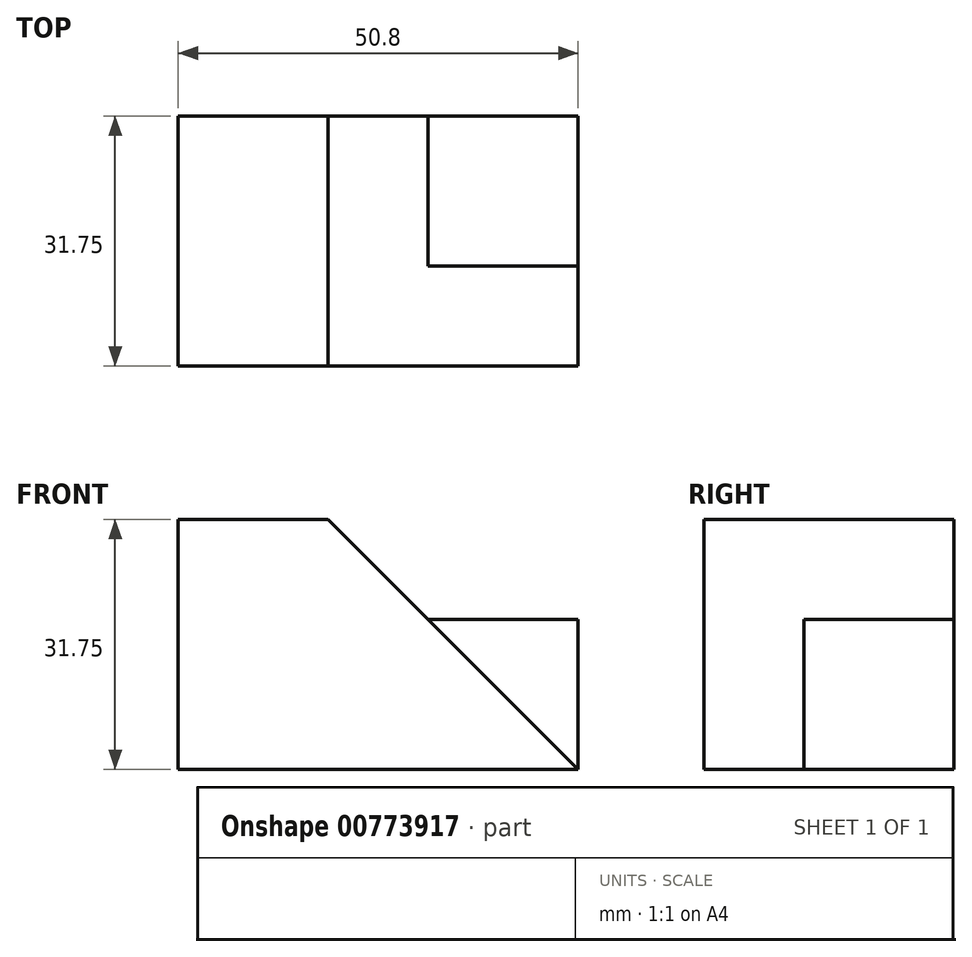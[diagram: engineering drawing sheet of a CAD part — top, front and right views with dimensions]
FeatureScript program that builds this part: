
annotation { "Feature Type Name" : "Feature", "Feature Type Description" : "" }
export const myFeature = defineFeature(function(context is Context, id is Id, definition is map)
    precondition{}
    {
        {
            var Q0;
            Q0=qCreatedBy(makeId("Front.planeOp"),FACE);
            var sketch = newSketch(context, id + "F0", { "sketchPlane" : qUnion([Q0])});
            skLineSegment(sketch, "E0", {"start": v(0, 0) * mm, "end": v(50.8, 0) * mm});
            skLineSegment(sketch, "E1", {"start": v(50.8, 0) * mm, "end": v(50.8, 31.75) * mm});
            skLineSegment(sketch, "E2", {"start": v(50.8, 31.75) * mm, "end": v(0, 31.75) * mm});
            skLineSegment(sketch, "E3", {"start": v(0, 0) * mm, "end": v(0, 31.75) * mm});
            skSolve(sketch);
        }
        {
            var Q0;
            Q0=makeQuery(id+"F0.imprint","IMPRINT",FACE,{"disambiguationData":[TD([[makeQuery(id+"F0.imprint","IMPRINT",EDGE,{"derivedFrom":sQuery(id+"F0.wireOp",EDGE,"E0")}),1.0]])]});
            extrude(context, id + "F1", {"entities" : qUnion([Q0]), "depth" : 31.75 * mm, "offsetDistance" : 25.4 * mm});
        }
        {
            var Q0;
            Q0=makeQuery(id+"F1.opExtrude","CAP_FACE",FACE,{"disambiguationData":[OSD([sQuery(id+"F0.wireOp",EDGE,"E0"),sQuery(id+"F0.wireOp",EDGE,"E1"),sQuery(id+"F0.wireOp",EDGE,"E2"),sQuery(id+"F0.wireOp",EDGE,"E3")])],"isStart":false});
            var sketch = newSketch(context, id + "F2", { "sketchPlane" : qUnion([Q0])});
            skLineSegment(sketch, "E4", {"start": v(0, 31.75) * mm, "end": v(19.05, 31.75) * mm});
            skLineSegment(sketch, "E5", {"start": v(19.05, 31.75) * mm, "end": v(50.8, 0) * mm});
            skSolve(sketch);
        }
        {
            var Q0;
            {var subQ0=sQuery(id+"F2.wireOp",EDGE,"E5");Q0=makeQuery(id+"F2.imprint","IMPRINT",FACE,{"disambiguationData":[TD([[makeQuery(id+"F2.imprint","IMPRINT",EDGE,{"derivedFrom":subQ0}),1.0]])]});}
            extrude(context, id + "F3", {"entities" : qUnion([Q0]), "operationType" : NewBodyOperationType.REMOVE, "oppositeDirection" : true, "depth" : 12.7 * mm, "offsetDistance" : 25.4 * mm});
        }
        {
            var Q0;
            Q0=makeQuery(id+"F3.boolean.opBoolean","COPY",FACE,{"derivedFrom":makeQuery(id+"F3.opExtrude","CAP_FACE",FACE,{"disambiguationData":[OSD([sQuery(id+"F0.wireOp",EDGE,"E1"),sQuery(id+"F0.wireOp",EDGE,"E2"),sQuery(id+"F2.wireOp",EDGE,"E5")])],"isStart":false})});
            var sketch = newSketch(context, id + "F4", { "sketchPlane" : qUnion([Q0])});
            skLineSegment(sketch, "E6", {"start": v(50.8, 0) * mm, "end": v(50.8, 19.05) * mm});
            skLineSegment(sketch, "E7", {"start": v(50.8, 19.05) * mm, "end": v(31.75, 19.05) * mm});
            skSolve(sketch);
        }
        {
            var Q0;
            {var subQ0=sQuery(id+"F4.wireOp",EDGE,"E7");Q0=makeQuery(id+"F4.imprint","IMPRINT",FACE,{"disambiguationData":[TD([[makeQuery(id+"F4.imprint","IMPRINT",EDGE,{"derivedFrom":subQ0}),-1.0]])]});}
            extrude(context, id + "F5", {"entities" : qUnion([Q0]), "operationType" : NewBodyOperationType.REMOVE, "oppositeDirection" : true, "depth" : 25.4 * mm, "offsetDistance" : 25.4 * mm});
        }
    });
